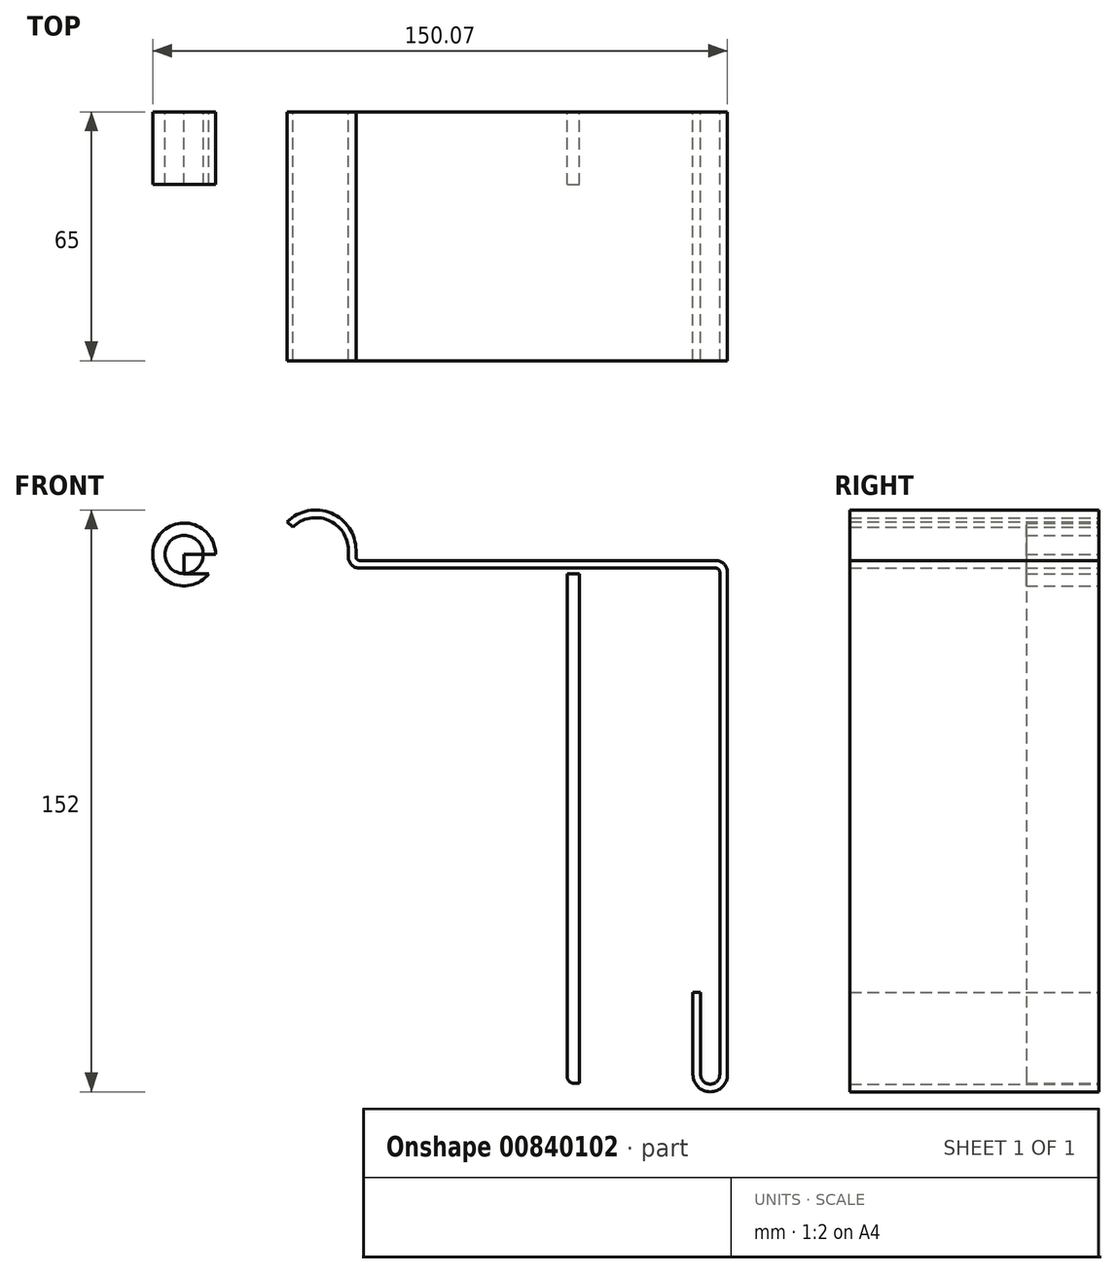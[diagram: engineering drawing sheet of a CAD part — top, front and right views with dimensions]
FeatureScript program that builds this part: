
annotation { "Feature Type Name" : "Feature", "Feature Type Description" : "" }
export const myFeature = defineFeature(function(context is Context, id is Id, definition is map)
    precondition{}
    {
        {
            var Q0;
            Q0=qCreatedBy(makeId("Front.planeOp"),FACE);
            var sketch = newSketch(context, id + "F0", { "sketchPlane" : qUnion([Q0])});
            skLineSegment(sketch, "E0.bottom", {"start": v(-50, 1.6) * mm, "end": v(50, 1.6) * mm});
            skLineSegment(sketch, "E0.top", {"start": v(-50, -1.6) * mm, "end": v(50, -1.6) * mm});
            skLineSegment(sketch, "E0.left", {"start": v(-50, 1.6) * mm, "end": v(-50, -1.6) * mm});
            skLineSegment(sketch, "E0.right", {"start": v(50, 1.6) * mm, "end": v(50, -1.6) * mm});
            skPoint(sketch, "E0.middle", {"position": v(0, 0) * mm});
            skPoint(sketch, "E1", {"position": v(-50, 6.6) * mm});
            skCircle(sketch, "E2", {"center": v(-50, 6.6) * mm, "radius": 5 * mm});
            skCircle(sketch, "E3", {"center": v(-50, 6.6) * mm, "radius": 8.2 * mm});
            skLineSegment(sketch, "E4.bottom", {"start": v(-50, 6.6) * mm, "end": v(-41.8, 6.6) * mm});
            skLineSegment(sketch, "E4.top", {"start": v(-50, 1.6) * mm, "end": v(-41.8, 1.6) * mm});
            skLineSegment(sketch, "E4.left", {"start": v(-50, 6.6) * mm, "end": v(-50, 1.6) * mm});
            skLineSegment(sketch, "E4.right", {"start": v(-41.8, 6.6) * mm, "end": v(-41.8, 1.6) * mm});
            skLineSegment(sketch, "E5.bottom", {"start": v(-50, 1.6) * mm, "end": v(-45, 1.6) * mm});
            skLineSegment(sketch, "E5.top", {"start": v(-50, 6.6) * mm, "end": v(-45, 6.6) * mm});
            skLineSegment(sketch, "E5.left", {"start": v(-50, 1.6) * mm, "end": v(-50, 6.6) * mm});
            skLineSegment(sketch, "E5.right", {"start": v(-45, 1.6) * mm, "end": v(-45, 6.6) * mm});
            skLineSegment(sketch, "E6.bottom", {"start": v(-45, 1.6) * mm, "end": v(-41.8, 1.6) * mm});
            skLineSegment(sketch, "E6.top", {"start": v(-45, 2.1) * mm, "end": v(-41.8, 2.1) * mm});
            skLineSegment(sketch, "E6.left", {"start": v(-45, 1.6) * mm, "end": v(-45, 2.1) * mm});
            skLineSegment(sketch, "E6.right", {"start": v(-41.8, 1.6) * mm, "end": v(-41.8, 2.1) * mm});
            skLineSegment(sketch, "E7.bottom", {"start": v(50, 1.6) * mm, "end": v(53.2, 1.6) * mm});
            skLineSegment(sketch, "E7.top", {"start": v(50, -131.6) * mm, "end": v(53.2, -131.6) * mm});
            skLineSegment(sketch, "E7.left", {"start": v(50, 1.6) * mm, "end": v(50, -131.6) * mm});
            skLineSegment(sketch, "E7.right", {"start": v(53.2, 1.6) * mm, "end": v(53.2, -131.6) * mm});
            skSolve(sketch);
        }
        {
            var Q0;
            {var subQ0=sQuery(id+"F0.wireOp",EDGE,"E0.left");Q0=makeQuery(id+"F0.imprint","IMPRINT",FACE,{"disambiguationData":[TD([[makeQuery(id+"F0.imprint","IMPRINT",EDGE,{"derivedFrom":subQ0}),-1.0]])]});}
            var Q1;
            {var subQ0=sQuery(id+"F0.wireOp",EDGE,"E4.bottom");Q1=makeQuery(id+"F0.imprint","IMPRINT",FACE,{"disambiguationData":[TD([[makeQuery(id+"F0.imprint","IMPRINT",EDGE,{"derivedFrom":subQ0}),-1.0]])]});}
            var Q2;
            {var subQ1=sQuery(id+"F0.wireOp",EDGE,"E0.bottom");Q2=makeQuery(id+"F0.imprint","IMPRINT",FACE,{"disambiguationData":[TD([[makeQuery(id+"F0.imprint","IMPRINT",EDGE,{"derivedFrom":subQ1}),-1.0]])]});}
            var Q3;
            {var subQ0=sQuery(id+"F0.wireOp",EDGE,"E0.left");Q3=makeQuery(id+"F0.imprint","IMPRINT",FACE,{"disambiguationData":[TD([[makeQuery(id+"F0.imprint","IMPRINT",EDGE,{"derivedFrom":subQ0}),1.0]])]});}
            var Q4;
            {var subQ0=sQuery(id+"F0.wireOp",EDGE,"E4.right");Q4=makeQuery(id+"F0.imprint","IMPRINT",FACE,{"disambiguationData":[TD([[makeQuery(id+"F0.imprint","IMPRINT",EDGE,{"derivedFrom":subQ0}),-1.0]])]});}
            var Q5;
            {var subQ3=sQuery(id+"F0.wireOp",EDGE,"E7.bottom");Q5=makeQuery(id+"F0.imprint","IMPRINT",FACE,{"disambiguationData":[TD([[makeQuery(id+"F0.imprint","IMPRINT",EDGE,{"derivedFrom":subQ3}),-1.0]])]});}
            extrude(context, id + "F1", {"entities" : qUnion([Q0, Q1, Q2, Q3, Q4, Q5]), "depth" : 19 * mm, "offsetDistance" : 25 * mm});
        }
        {
            var Q0;
            Q0=makeQuery(id+"F1.opExtrude","SWEPT_EDGE",EDGE,{"disambiguationData":[OSD([sQuery(id+"F0.wireOp",EDGE,"E0.top"),sQuery(id+"F0.wireOp",EDGE,"E7.left")])]});
            fillet(context, id + "F2", {"entities" : qUnion([Q0]), "radius" : 2 * mm, "tangentPropagation" : true, "allowEdgeOverflow" : false});
        }
        {
            var Q0;
            Q0=makeQuery(id+"F1.opExtrude","CAP_FACE",FACE,{"disambiguationData":[OSD([sQuery(id+"F0.wireOp",EDGE,"E0.bottom"),sQuery(id+"F0.wireOp",EDGE,"E0.top"),sQuery(id+"F0.wireOp",EDGE,"E2"),sQuery(id+"F0.wireOp",EDGE,"E3"),sQuery(id+"F0.wireOp",EDGE,"E4.right"),sQuery(id+"F0.wireOp",EDGE,"E5.bottom"),sQuery(id+"F0.wireOp",EDGE,"E5.right"),sQuery(id+"F0.wireOp",EDGE,"E6.bottom"),sQuery(id+"F0.wireOp",EDGE,"E6.top"),sQuery(id+"F0.wireOp",EDGE,"E7.bottom"),sQuery(id+"F0.wireOp",EDGE,"E7.top"),sQuery(id+"F0.wireOp",EDGE,"E7.left"),sQuery(id+"F0.wireOp",EDGE,"E7.right")])],"isStart":false});
            extrude(context, id + "F3", {"entities" : qUnion([Q0]), "operationType" : NewBodyOperationType.REMOVE, "oppositeDirection" : true, "depth" : 18 * mm, "offsetDistance" : 25 * mm});
        }
        {
            var Q0;
            Q0=makeQuery(id+"F3.boolean.opBoolean","COPY",FACE,{"derivedFrom":makeQuery(id+"F3.opExtrude","CAP_FACE",FACE,{"disambiguationData":[OSD([sQuery(id+"F0.wireOp",EDGE,"E0.bottom"),sQuery(id+"F0.wireOp",EDGE,"E0.top"),sQuery(id+"F0.wireOp",EDGE,"E2"),sQuery(id+"F0.wireOp",EDGE,"E3"),sQuery(id+"F0.wireOp",EDGE,"E4.right"),sQuery(id+"F0.wireOp",EDGE,"E5.bottom"),sQuery(id+"F0.wireOp",EDGE,"E5.right"),sQuery(id+"F0.wireOp",EDGE,"E6.bottom"),sQuery(id+"F0.wireOp",EDGE,"E6.top"),sQuery(id+"F0.wireOp",EDGE,"E7.bottom"),sQuery(id+"F0.wireOp",EDGE,"E7.top"),sQuery(id+"F0.wireOp",EDGE,"E7.left"),sQuery(id+"F0.wireOp",EDGE,"E7.right")])],"isStart":false})});
            extrude(context, id + "F4", {"entities" : qUnion([Q0]), "operationType" : NewBodyOperationType.REMOVE, "oppositeDirection" : true, "depth" : 1 * mm, "offsetDistance" : 25 * mm});
        }
        {
            var Q0;
            Q0=qCreatedBy(makeId("Front.planeOp"),FACE);
            var sketch = newSketch(context, id + "F5", { "sketchPlane" : qUnion([Q0])});
            skLineSegment(sketch, "E8.bottom", {"start": v(-10.63, 7.7) * mm, "end": v(-10.63, 7.7) * mm});
            skLineSegment(sketch, "E9.right", {"start": v(-5.13, 6) * mm, "end": v(-5.13, 7.7) * mm});
            skLineSegment(sketch, "E10.trimOffspring", {"start": v(-7.43, 7.7) * mm, "end": v(-7.43, 7.7) * mm});
            skLineSegment(sketch, "E11", {"start": v(-4.13, 5) * mm, "end": v(88.87, 5) * mm});
            skLineSegment(sketch, "E12", {"start": v(-7.13, 7.7) * mm, "end": v(-7.13, 6) * mm});
            skLineSegment(sketch, "E13", {"start": v(-4.13, 3) * mm, "end": v(88.87, 3) * mm});
            skLineSegment(sketch, "E14", {"start": v(-21.64, 13.72) * mm, "end": v(-23.05, 15.13) * mm});
            skPoint(sketch, "E15", {"position": v(-4.13, 6) * mm});
            skArc(sketch, "E16", {"start": v(-5.13, 6) * mm, "mid": v(-4.84, 5.3) * mm, "end": v(-4.13, 5) * mm});
            skArc(sketch, "E17", {"start": v(-7.13, 6) * mm, "mid": v(-6.25, 3.88) * mm, "end": v(-4.13, 3) * mm});
            skPoint(sketch, "E18.orphan", {"position": v(-5.13, 5) * mm});
            skPoint(sketch, "E19", {"position": v(-15.63, 7.7) * mm});
            skArc(sketch, "E20", {"start": v(-7.13, 7.7) * mm, "mid": v(-12.38, 15.56) * mm, "end": v(-21.64, 13.72) * mm});
            skArc(sketch, "E21", {"start": v(-5.13, 7.7) * mm, "mid": v(-11.61, 17.4) * mm, "end": v(-23.05, 15.13) * mm});
            skPoint(sketch, "E22", {"position": v(88.87, 2) * mm});
            skArc(sketch, "E23", {"start": v(89.87, 2) * mm, "mid": v(89.58, 2.71) * mm, "end": v(88.87, 3) * mm});
            skArc(sketch, "E24.trimOffspring", {"start": v(91.87, 2) * mm, "mid": v(91, 4.13) * mm, "end": v(88.87, 5) * mm});
            skLineSegment(sketch, "E25", {"start": v(82.87, -107.8) * mm, "end": v(84.87, -107.8) * mm});
            skPoint(sketch, "E26", {"position": v(87.37, -129.3) * mm});
            skArc(sketch, "E27", {"start": v(84.87, -129.3) * mm, "mid": v(87.37, -131.8) * mm, "end": v(89.87, -129.3) * mm});
            skArc(sketch, "E28", {"start": v(82.87, -129.3) * mm, "mid": v(87.37, -133.8) * mm, "end": v(91.87, -129.3) * mm});
            skLineSegment(sketch, "E29", {"start": v(82.87, -107.8) * mm, "end": v(82.87, -129.3) * mm});
            skLineSegment(sketch, "E30", {"start": v(84.87, -107.8) * mm, "end": v(84.87, -129.3) * mm});
            skLineSegment(sketch, "E31", {"start": v(89.87, 2) * mm, "end": v(89.87, -129.3) * mm});
            skLineSegment(sketch, "E32", {"start": v(91.87, -129.3) * mm, "end": v(91.87, 2) * mm});
            skSolve(sketch);
        }
        {
            var Q0;
            Q0=qSketchRegion(id+"F5",true);
            extrude(context, id + "F6", {"entities" : qUnion([Q0]), "depth" : 65 * mm, "offsetDistance" : 25 * mm});
        }
    });
